# Revit family: 4069443 Sylvania Lighting Fixture CUBE WALL1 175LM QE LED 4K AL
name_source: partatom
category: Lighting Fixtures
revit_build: Autodesk Revit 2016 (Build: 20150220_1215(x64)
units: mm (PartAtom-declared; Revit-internal decimal feet)

## family parameters
Cut with Voids When Loaded = No
Host = Face
Light Source = No
OmniClass Number = 23.80.70.00
OmniClass Title = Lighting
Part Type = Normal
Room Calculation Point = No
Round Connector Dimension = Use Diameter
Shared = No

## types (1)
- 4069443 CUBE/W1 175LM QE LED 4K AL
    Apparent Load = 8 VA
    Assembly Code = D5020200
    AssetType = Fixed
    CapThickness_SYL = 10 mm  [stored 0.0328084 ft]
    Chamfer_SYL = 1 mm  [stored 0.00328084 ft]
    Cost = 0 $
    Default Elevation = 1219 mm
    Description = Wall mounted LED luminaireCorrosion resistant die-cast aluminium, 175lm, 7.5W, 23lm/W, 4000K, CRI80+, 55°, non dimmable, IP65, IK07,  (HxWxD) 90x90x90mm, 3 step MacAdam ellipse, Class I, 220-240, A++ A+ A
    DiffuserFromFront_SYL = 18 mm  [stored 0.0590551 ft]
    DiffuserFromSide_SYL = 10 mm  [stored 0.0328084 ft]
    DiffuserHeightHalf_SYL = 20 mm
    DocumentationLiterature = http://www.sylvania-lighting.com
    DurationUnit = hours
    ElectricShockClassification = Class I
    ExpectedLife = 50000
    IfcExportAs = IfcLightFixtureType
    IfcExportType = IfcLightFixtureType
    ImpactProtectionIndex = IK07
    IngressProtection = IP65
    Keynote = 16500
    Lamp = LED
    LampColourRenderingIndex = 80
    LampColourTemperature = 4000 K
    LampNominalLuminous = 175 lm
    LampsType = LED
    LightOutputRatio = 100
    LuminousEfficacy = 23.33 lm/W
    Manufacturer = Feilo Sylvania
    ManufacturerName = Feilo Sylvania
    Material = corrosion resistant die-cast aluminium housing, safety tempered glass diffuser
    Material_1_SYL = Aluminum 7175 T73 0 Hot Formed
    Material_2_SYL = <By Category>
    Material_3_SYL = <By Category>
    Material_4_SYL = <By Category>
    Model = CUBE/WALL1 175LM QE LED 4K AL
    ModelNumber = 4069443
    ModelReference = CUBE/WALL1 175LM QE LED 4K AL
    Name = CUBE/WALL1 175LM QE LED 4K AL
    NominalHeight = 90 mm  [stored 0.295276 ft]
    NominalLength = 90 mm  [stored 0.295276 ft]
    NominalWidth = 0 mm  [stored 0 ft]
    PowerConsumption = 7.5 W
    PowerFactor = 0
    Type Image = <None>
    TypeLightDown_SYL = Cube Light Source : 4069443 CUBE/W1 175LM QE LED 4K AL
    TypeLightLeft_SYL = Cube Light Source : 4069443 CUBE/W1 175LM QE LED 4K AL
    TypeLightRight_SYL = Cube Light Source : 4069443 CUBE/W1 175LM QE LED 4K AL
    TypeLightUp_SYL = Cube Light Source : 4069443 CUBE/W1 175LM QE LED 4K AL
    TypeName = CUBE/WALL1 175LM QE LED 4K AL
    URL = http://www.sylvania-lighting.com
    Voltage = 0 V
    Weight = 0.75 kg
    Width_SYL = 90 mm  [stored 0.295276 ft]

note: [stored X ft] marks values corroborated as IEEE doubles in the binary element streams (Revit-internal decimal feet)

## geometry (parser evidence)
native form markers: Sweep x6
no freeform markers — native parametric forms only
